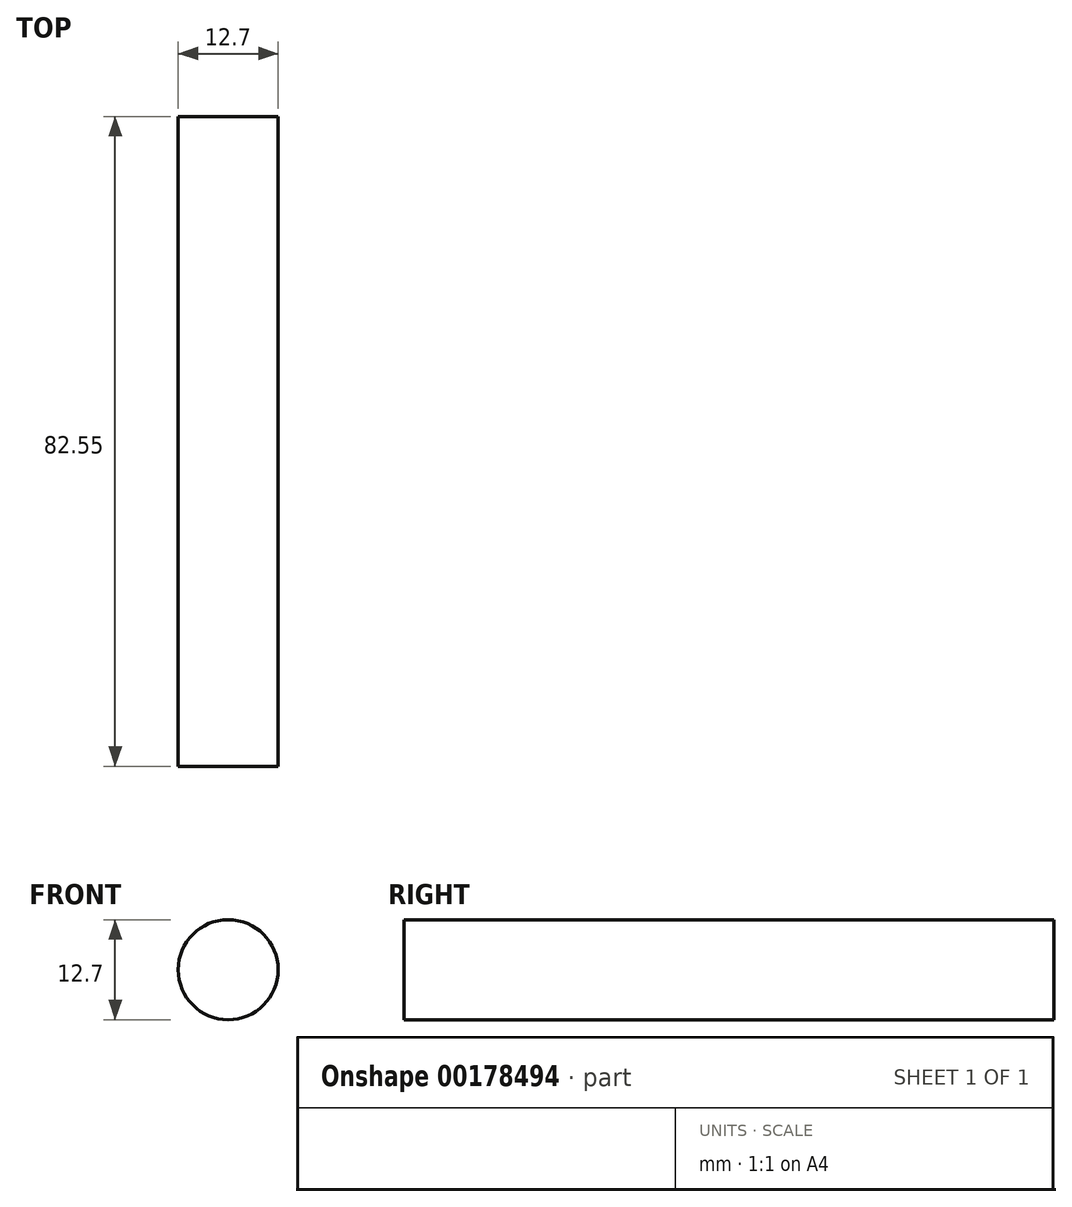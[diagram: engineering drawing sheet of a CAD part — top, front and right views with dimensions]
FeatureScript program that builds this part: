
annotation { "Feature Type Name" : "Feature", "Feature Type Description" : "" }
export const myFeature = defineFeature(function(context is Context, id is Id, definition is map)
    precondition{}
    {
        {
            var Q0;
            Q0=qCreatedBy(makeId("Front.planeOp"),FACE);
            var sketch = newSketch(context, id + "F0", { "sketchPlane" : qUnion([Q0])});
            skCircle(sketch, "E0", {"center": v(0, 0) * mm, "radius": 6.35 * mm});
            skSolve(sketch);
        }
        {
            var Q0;
            Q0=makeQuery(id+"F0.imprint","IMPRINT",FACE,{"disambiguationData":[TD([[makeQuery(id+"F0.imprint","IMPRINT",EDGE,{"derivedFrom":sQuery(id+"F0.wireOp",EDGE,"E0")}),1.0]])]});
            extrude(context, id + "F1", {"entities" : qUnion([Q0]), "depth" : 82.55 * mm});
        }
    });
